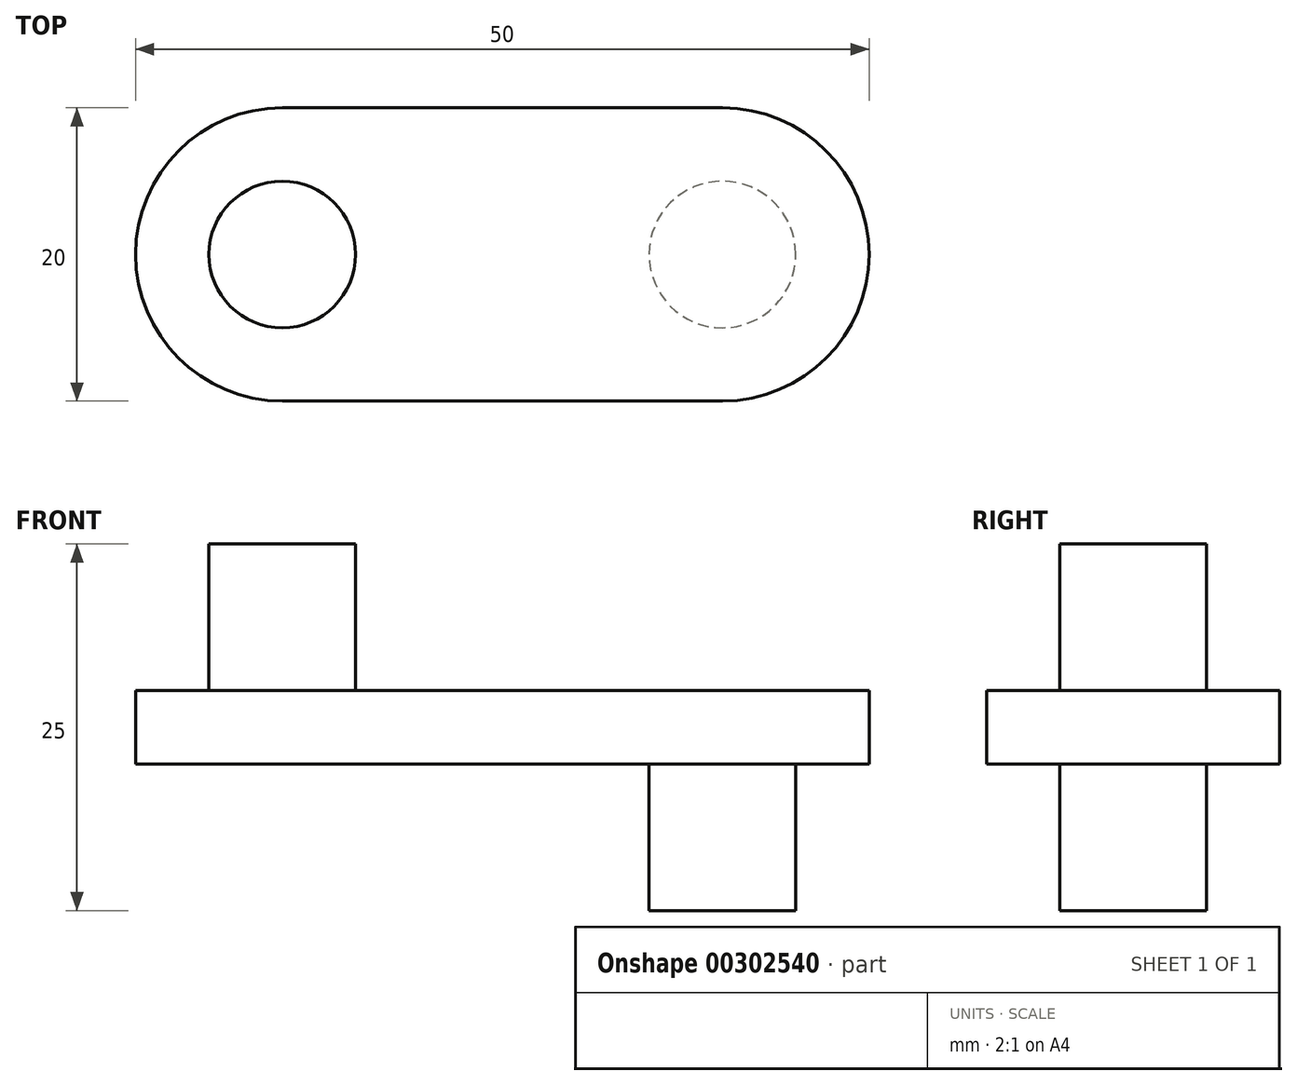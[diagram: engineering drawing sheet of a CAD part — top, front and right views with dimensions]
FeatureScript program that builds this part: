
annotation { "Feature Type Name" : "Feature", "Feature Type Description" : "" }
export const myFeature = defineFeature(function(context is Context, id is Id, definition is map)
    precondition{}
    {
        {
            var Q0;
            Q0=qCreatedBy(makeId("Top.planeOp"),FACE);
            var sketch = newSketch(context, id + "F0", { "sketchPlane" : qUnion([Q0])});
            skArc(sketch, "E0", {"start": v(0, 20) * mm, "mid": v(-10, 10) * mm, "end": v(0, 0) * mm});
            skLineSegment(sketch, "E1", {"start": v(0, 20) * mm, "end": v(30, 20) * mm});
            skLineSegment(sketch, "E2", {"start": v(0, 0) * mm, "end": v(30, 0) * mm});
            skArc(sketch, "E3", {"start": v(30, 0) * mm, "mid": v(40, 10) * mm, "end": v(30, 20) * mm});
            skCircle(sketch, "E4", {"center": v(0, 10) * mm, "radius": 5 * mm});
            skCircle(sketch, "E5", {"center": v(30, 10) * mm, "radius": 5 * mm});
            skSolve(sketch);
        }
        {
            var Q0;
            Q0=makeQuery(id+"F0.imprint","IMPRINT",FACE,{"disambiguationData":[TD([[makeQuery(id+"F0.imprint","IMPRINT",EDGE,{"derivedFrom":sQuery(id+"F0.wireOp",EDGE,"E0")}),1.0]])]});
            var Q1;
            Q1=makeQuery(id+"F0.imprint","IMPRINT",FACE,{"disambiguationData":[TD([[makeQuery(id+"F0.imprint","IMPRINT",EDGE,{"derivedFrom":sQuery(id+"F0.wireOp",EDGE,"E4")}),1.0]])]});
            extrude(context, id + "F1", {"entities" : qUnion([Q0, Q1]), "oppositeDirection" : true, "depth" : 5 * mm});
        }
        {
            var Q0;
            Q0=makeQuery(id+"F0.imprint","IMPRINT",FACE,{"disambiguationData":[TD([[makeQuery(id+"F0.imprint","IMPRINT",EDGE,{"derivedFrom":sQuery(id+"F0.wireOp",EDGE,"E5")}),1.0]])]});
            extrude(context, id + "F2", {"entities" : qUnion([Q0]), "operationType" : NewBodyOperationType.ADD, "oppositeDirection" : true, "depth" : 15 * mm});
        }
        {
            var Q0;
            Q0=makeQuery(id+"F0.imprint","IMPRINT",FACE,{"disambiguationData":[TD([[makeQuery(id+"F0.imprint","IMPRINT",EDGE,{"derivedFrom":sQuery(id+"F0.wireOp",EDGE,"E4")}),1.0]])]});
            extrude(context, id + "F3", {"entities" : qUnion([Q0]), "operationType" : NewBodyOperationType.ADD, "depth" : 10 * mm});
        }
    });
